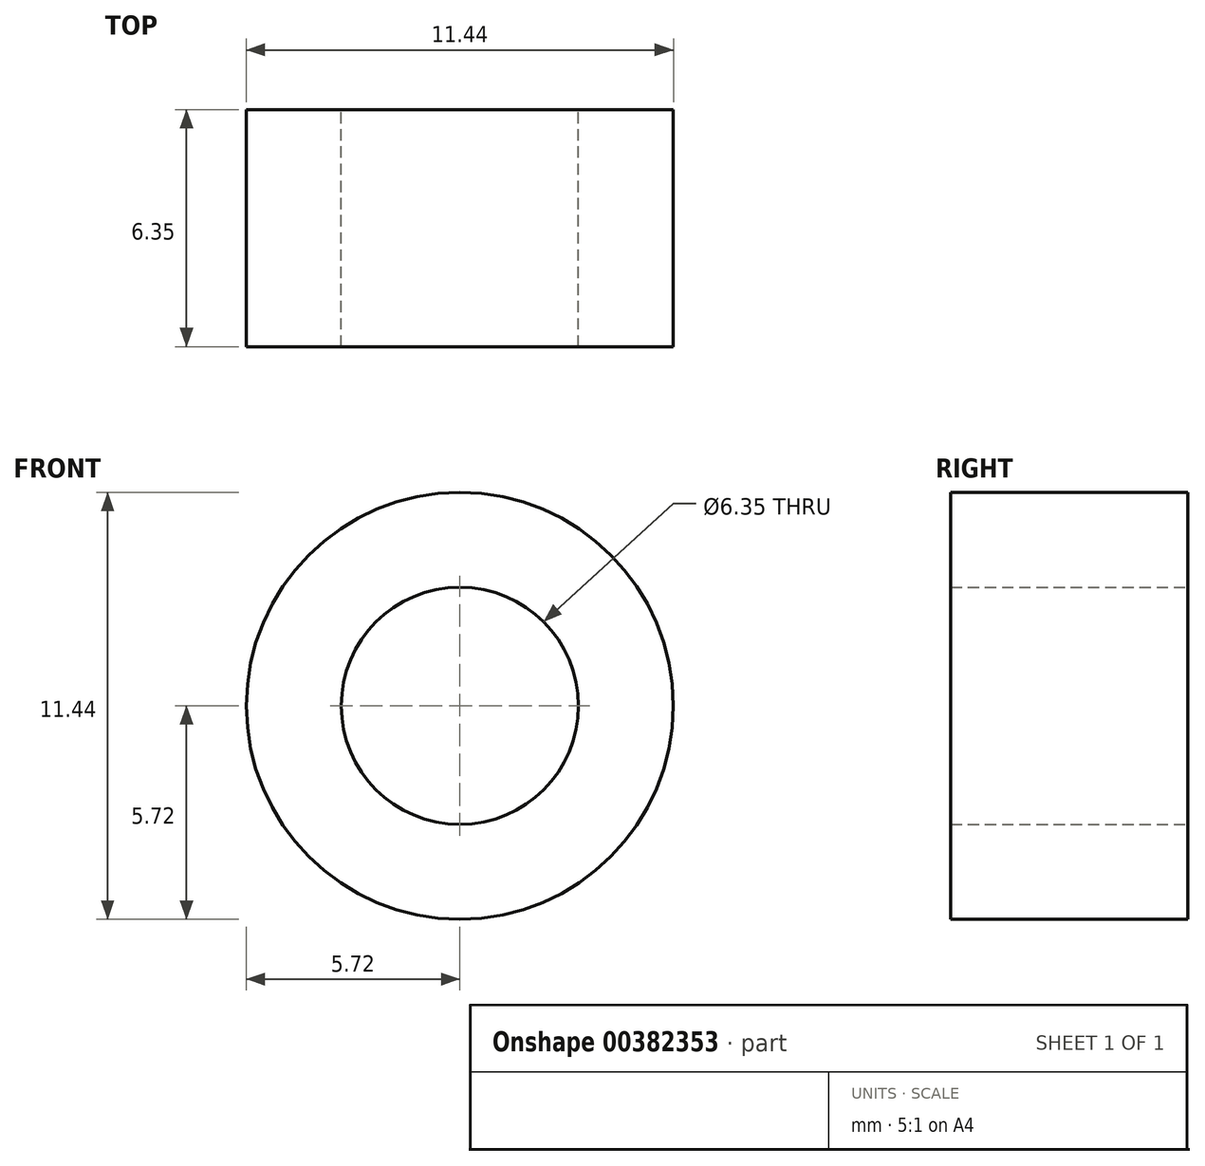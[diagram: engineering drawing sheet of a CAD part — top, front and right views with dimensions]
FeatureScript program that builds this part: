
annotation { "Feature Type Name" : "Feature", "Feature Type Description" : "" }
export const myFeature = defineFeature(function(context is Context, id is Id, definition is map)
    precondition{}
    {
        {
            var Q0;
            Q0=qCreatedBy(makeId("Front.planeOp"),FACE);
            var sketch = newSketch(context, id + "F0", { "sketchPlane" : qUnion([Q0])});
            skCircle(sketch, "E0", {"center": v(0, 0) * mm, "radius": 3.18 * mm});
            skCircle(sketch, "E1", {"center": v(0, 0) * mm, "radius": 5.72 * mm});
            skSolve(sketch);
        }
        {
            var Q0;
            Q0 = qSketchRegion(id + "F0", true);
            extrude(context, id + "F1", {"entities" : qUnion([Q0]), "depth" : 6.35 * mm});
        }
    });
